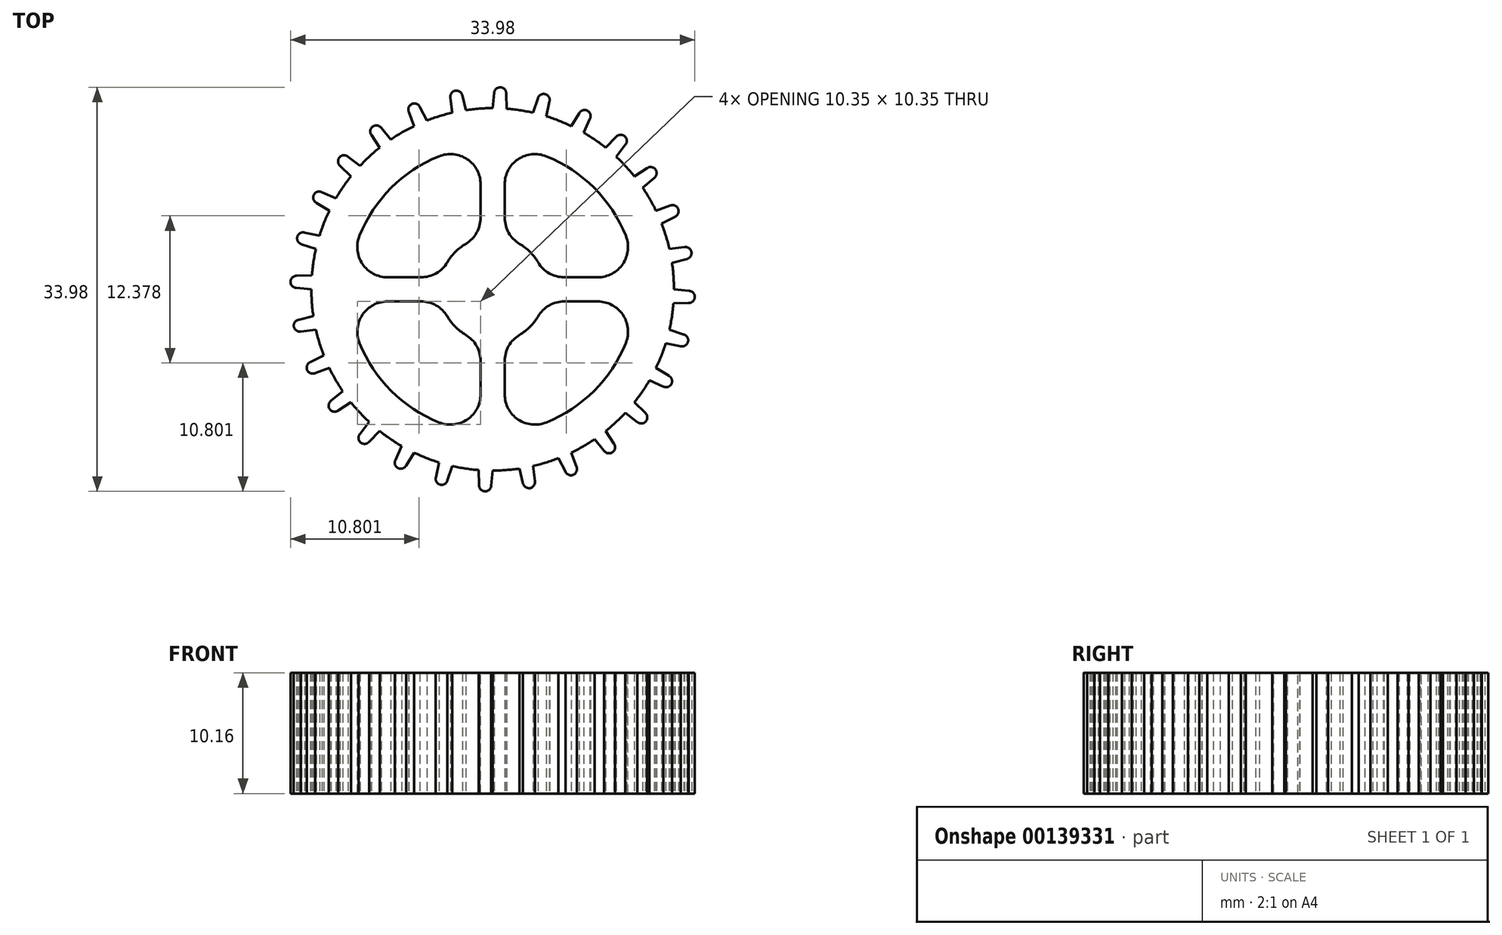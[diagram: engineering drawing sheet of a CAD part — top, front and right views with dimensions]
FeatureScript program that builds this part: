
annotation { "Feature Type Name" : "Feature", "Feature Type Description" : "" }
export const myFeature = defineFeature(function(context is Context, id is Id, definition is map)
    precondition{}
    {
        {
            var Q0;
            Q0=qCreatedBy(makeId("Top.planeOp"),FACE);
            var sketch = newSketch(context, id + "F0", { "sketchPlane" : qUnion([Q0])});
            skCircle(sketch, "E0", {"center": v(0, 0) * mm, "radius": 15.24 * mm});
            skLineSegment(sketch, "E1", {"start": v(0, 15.24) * mm, "end": v(1.17, 15.2) * mm});
            skLineSegment(sketch, "E2", {"start": v(1.17, 15.2) * mm, "end": v(1.14, 16.46) * mm});
            skLineSegment(sketch, "E3", {"start": v(0.13, 16.5) * mm, "end": v(0, 15.24) * mm});
            skArc(sketch, "E4", {"start": v(1.14, 16.46) * mm, "mid": v(0.65, 17) * mm, "end": v(0.13, 16.5) * mm});
            skLineSegment(sketch, "E5.1.0", {"start": v(-2.24, 15.07) * mm, "end": v(-2.55, 16.3) * mm});
            skArc(sketch, "E5.1.1", {"start": v(-2.55, 16.3) * mm, "mid": v(-3.14, 16.71) * mm, "end": v(-3.55, 16.12) * mm});
            skLineSegment(sketch, "E5.1.2", {"start": v(-3.55, 16.12) * mm, "end": v(-3.4, 14.86) * mm});
            skLineSegment(sketch, "E5.2.0", {"start": v(-5.54, 14.2) * mm, "end": v(-6.12, 15.33) * mm});
            skArc(sketch, "E5.2.1", {"start": v(-6.12, 15.33) * mm, "mid": v(-6.78, 15.6) * mm, "end": v(-7.05, 14.92) * mm});
            skLineSegment(sketch, "E5.2.2", {"start": v(-7.05, 14.92) * mm, "end": v(-6.61, 13.73) * mm});
            skLineSegment(sketch, "E5.3.0", {"start": v(-8.56, 12.6) * mm, "end": v(-9.37, 13.58) * mm});
            skArc(sketch, "E5.3.1", {"start": v(-9.37, 13.58) * mm, "mid": v(-10.08, 13.7) * mm, "end": v(-10.2, 12.98) * mm});
            skLineSegment(sketch, "E5.3.2", {"start": v(-10.2, 12.98) * mm, "end": v(-9.5, 11.92) * mm});
            skLineSegment(sketch, "E5.4.0", {"start": v(-11.15, 10.39) * mm, "end": v(-12.16, 11.16) * mm});
            skArc(sketch, "E5.4.1", {"start": v(-12.16, 11.16) * mm, "mid": v(-12.88, 11.1) * mm, "end": v(-12.82, 10.39) * mm});
            skLineSegment(sketch, "E5.4.2", {"start": v(-12.82, 10.39) * mm, "end": v(-11.92, 9.5) * mm});
            skLineSegment(sketch, "E5.5.0", {"start": v(-13.18, 7.65) * mm, "end": v(-14.34, 8.17) * mm});
            skArc(sketch, "E5.5.1", {"start": v(-14.34, 8.17) * mm, "mid": v(-15.03, 7.96) * mm, "end": v(-14.81, 7.27) * mm});
            skLineSegment(sketch, "E5.5.2", {"start": v(-14.81, 7.27) * mm, "end": v(-13.73, 6.61) * mm});
            skLineSegment(sketch, "E5.6.0", {"start": v(-14.55, 4.52) * mm, "end": v(-15.8, 4.78) * mm});
            skArc(sketch, "E5.6.1", {"start": v(-15.8, 4.78) * mm, "mid": v(-16.42, 4.42) * mm, "end": v(-16.06, 3.8) * mm});
            skLineSegment(sketch, "E5.6.2", {"start": v(-16.06, 3.8) * mm, "end": v(-14.86, 3.4) * mm});
            skLineSegment(sketch, "E5.7.0", {"start": v(-15.2, 1.17) * mm, "end": v(-16.46, 1.14) * mm});
            skArc(sketch, "E5.7.1", {"start": v(-16.46, 1.14) * mm, "mid": v(-17, 0.65) * mm, "end": v(-16.5, 0.13) * mm});
            skLineSegment(sketch, "E5.7.2", {"start": v(-16.5, 0.13) * mm, "end": v(-15.24, 0) * mm});
            skLineSegment(sketch, "E5.8.0", {"start": v(-15.07, -2.24) * mm, "end": v(-16.3, -2.55) * mm});
            skArc(sketch, "E5.8.1", {"start": v(-16.3, -2.55) * mm, "mid": v(-16.71, -3.14) * mm, "end": v(-16.12, -3.55) * mm});
            skLineSegment(sketch, "E5.8.2", {"start": v(-16.12, -3.55) * mm, "end": v(-14.86, -3.4) * mm});
            skLineSegment(sketch, "E5.9.0", {"start": v(-14.2, -5.54) * mm, "end": v(-15.33, -6.12) * mm});
            skArc(sketch, "E5.9.1", {"start": v(-15.33, -6.12) * mm, "mid": v(-15.6, -6.78) * mm, "end": v(-14.92, -7.05) * mm});
            skLineSegment(sketch, "E5.9.2", {"start": v(-14.92, -7.05) * mm, "end": v(-13.73, -6.61) * mm});
            skLineSegment(sketch, "E5.10.0", {"start": v(-12.6, -8.56) * mm, "end": v(-13.58, -9.37) * mm});
            skArc(sketch, "E5.10.1", {"start": v(-13.58, -9.37) * mm, "mid": v(-13.7, -10.08) * mm, "end": v(-12.98, -10.2) * mm});
            skLineSegment(sketch, "E5.10.2", {"start": v(-12.98, -10.2) * mm, "end": v(-11.92, -9.5) * mm});
            skLineSegment(sketch, "E5.11.0", {"start": v(-10.39, -11.15) * mm, "end": v(-11.16, -12.16) * mm});
            skArc(sketch, "E5.11.1", {"start": v(-11.16, -12.16) * mm, "mid": v(-11.1, -12.88) * mm, "end": v(-10.39, -12.82) * mm});
            skLineSegment(sketch, "E5.11.2", {"start": v(-10.39, -12.82) * mm, "end": v(-9.5, -11.92) * mm});
            skLineSegment(sketch, "E5.12.0", {"start": v(-7.65, -13.18) * mm, "end": v(-8.17, -14.34) * mm});
            skArc(sketch, "E5.12.1", {"start": v(-8.17, -14.34) * mm, "mid": v(-7.96, -15.03) * mm, "end": v(-7.27, -14.81) * mm});
            skLineSegment(sketch, "E5.12.2", {"start": v(-7.27, -14.81) * mm, "end": v(-6.61, -13.73) * mm});
            skLineSegment(sketch, "E5.13.0", {"start": v(-4.52, -14.55) * mm, "end": v(-4.78, -15.8) * mm});
            skArc(sketch, "E5.13.1", {"start": v(-4.78, -15.8) * mm, "mid": v(-4.42, -16.42) * mm, "end": v(-3.8, -16.06) * mm});
            skLineSegment(sketch, "E5.13.2", {"start": v(-3.8, -16.06) * mm, "end": v(-3.4, -14.86) * mm});
            skLineSegment(sketch, "E5.14.0", {"start": v(-1.17, -15.2) * mm, "end": v(-1.14, -16.46) * mm});
            skArc(sketch, "E5.14.1", {"start": v(-1.14, -16.46) * mm, "mid": v(-0.65, -17) * mm, "end": v(-0.13, -16.5) * mm});
            skLineSegment(sketch, "E5.14.2", {"start": v(-0.13, -16.5) * mm, "end": v(0, -15.24) * mm});
            skLineSegment(sketch, "E5.15.0", {"start": v(2.24, -15.07) * mm, "end": v(2.55, -16.3) * mm});
            skArc(sketch, "E5.15.1", {"start": v(2.55, -16.3) * mm, "mid": v(3.14, -16.71) * mm, "end": v(3.55, -16.12) * mm});
            skLineSegment(sketch, "E5.15.2", {"start": v(3.55, -16.12) * mm, "end": v(3.4, -14.86) * mm});
            skLineSegment(sketch, "E5.16.0", {"start": v(5.54, -14.2) * mm, "end": v(6.12, -15.33) * mm});
            skArc(sketch, "E5.16.1", {"start": v(6.12, -15.33) * mm, "mid": v(6.78, -15.6) * mm, "end": v(7.05, -14.92) * mm});
            skLineSegment(sketch, "E5.16.2", {"start": v(7.05, -14.92) * mm, "end": v(6.61, -13.73) * mm});
            skLineSegment(sketch, "E5.17.0", {"start": v(8.56, -12.6) * mm, "end": v(9.37, -13.58) * mm});
            skArc(sketch, "E5.17.1", {"start": v(9.37, -13.58) * mm, "mid": v(10.08, -13.7) * mm, "end": v(10.2, -12.98) * mm});
            skLineSegment(sketch, "E5.17.2", {"start": v(10.2, -12.98) * mm, "end": v(9.5, -11.92) * mm});
            skLineSegment(sketch, "E5.18.0", {"start": v(11.15, -10.39) * mm, "end": v(12.16, -11.16) * mm});
            skArc(sketch, "E5.18.1", {"start": v(12.16, -11.16) * mm, "mid": v(12.88, -11.1) * mm, "end": v(12.82, -10.39) * mm});
            skLineSegment(sketch, "E5.18.2", {"start": v(12.82, -10.39) * mm, "end": v(11.92, -9.5) * mm});
            skLineSegment(sketch, "E5.19.0", {"start": v(13.18, -7.65) * mm, "end": v(14.34, -8.17) * mm});
            skArc(sketch, "E5.19.1", {"start": v(14.34, -8.17) * mm, "mid": v(15.03, -7.96) * mm, "end": v(14.81, -7.27) * mm});
            skLineSegment(sketch, "E5.19.2", {"start": v(14.81, -7.27) * mm, "end": v(13.73, -6.61) * mm});
            skLineSegment(sketch, "E5.20.0", {"start": v(14.55, -4.52) * mm, "end": v(15.8, -4.78) * mm});
            skArc(sketch, "E5.20.1", {"start": v(15.8, -4.78) * mm, "mid": v(16.42, -4.42) * mm, "end": v(16.06, -3.8) * mm});
            skLineSegment(sketch, "E5.20.2", {"start": v(16.06, -3.8) * mm, "end": v(14.86, -3.4) * mm});
            skLineSegment(sketch, "E5.21.0", {"start": v(15.2, -1.17) * mm, "end": v(16.46, -1.14) * mm});
            skArc(sketch, "E5.21.1", {"start": v(16.46, -1.14) * mm, "mid": v(17, -0.65) * mm, "end": v(16.5, -0.13) * mm});
            skLineSegment(sketch, "E5.21.2", {"start": v(16.5, -0.13) * mm, "end": v(15.24, 0) * mm});
            skLineSegment(sketch, "E5.22.0", {"start": v(15.07, 2.24) * mm, "end": v(16.3, 2.55) * mm});
            skArc(sketch, "E5.22.1", {"start": v(16.3, 2.55) * mm, "mid": v(16.71, 3.14) * mm, "end": v(16.12, 3.55) * mm});
            skLineSegment(sketch, "E5.22.2", {"start": v(16.12, 3.55) * mm, "end": v(14.86, 3.4) * mm});
            skLineSegment(sketch, "E5.23.0", {"start": v(14.2, 5.54) * mm, "end": v(15.33, 6.12) * mm});
            skArc(sketch, "E5.23.1", {"start": v(15.33, 6.12) * mm, "mid": v(15.6, 6.78) * mm, "end": v(14.92, 7.05) * mm});
            skLineSegment(sketch, "E5.23.2", {"start": v(14.92, 7.05) * mm, "end": v(13.73, 6.61) * mm});
            skLineSegment(sketch, "E5.24.0", {"start": v(12.6, 8.56) * mm, "end": v(13.58, 9.37) * mm});
            skArc(sketch, "E5.24.1", {"start": v(13.58, 9.37) * mm, "mid": v(13.7, 10.08) * mm, "end": v(12.98, 10.2) * mm});
            skLineSegment(sketch, "E5.24.2", {"start": v(12.98, 10.2) * mm, "end": v(11.92, 9.5) * mm});
            skLineSegment(sketch, "E5.25.0", {"start": v(10.39, 11.15) * mm, "end": v(11.16, 12.16) * mm});
            skArc(sketch, "E5.25.1", {"start": v(11.16, 12.16) * mm, "mid": v(11.1, 12.88) * mm, "end": v(10.39, 12.82) * mm});
            skLineSegment(sketch, "E5.25.2", {"start": v(10.39, 12.82) * mm, "end": v(9.5, 11.92) * mm});
            skLineSegment(sketch, "E5.26.0", {"start": v(7.65, 13.18) * mm, "end": v(8.17, 14.34) * mm});
            skArc(sketch, "E5.26.1", {"start": v(8.17, 14.34) * mm, "mid": v(7.96, 15.03) * mm, "end": v(7.27, 14.81) * mm});
            skLineSegment(sketch, "E5.26.2", {"start": v(7.27, 14.81) * mm, "end": v(6.61, 13.73) * mm});
            skLineSegment(sketch, "E5.27.0", {"start": v(4.52, 14.55) * mm, "end": v(4.78, 15.8) * mm});
            skArc(sketch, "E5.27.1", {"start": v(4.78, 15.8) * mm, "mid": v(4.42, 16.42) * mm, "end": v(3.8, 16.06) * mm});
            skLineSegment(sketch, "E5.27.2", {"start": v(3.8, 16.06) * mm, "end": v(3.4, 14.86) * mm});
            skSolve(sketch);
        }
        {
            var Q0;
            Q0 = qSketchRegion(id + "F0", true);
            extrude(context, id + "F1", {"entities" : qUnion([Q0]), "depth" : 10.16 * mm});
        }
        {
            var Q0;
            Q0=makeQuery(id+"F1.opExtrude","CAP_FACE",FACE,{"disambiguationData":[OSD([sQuery(id+"F0.wireOp",EDGE,"E0"),sQuery(id+"F0.wireOp",EDGE,"E2"),sQuery(id+"F0.wireOp",EDGE,"E3"),sQuery(id+"F0.wireOp",EDGE,"E4"),sQuery(id+"F0.wireOp",EDGE,"E5.1.0"),sQuery(id+"F0.wireOp",EDGE,"E5.1.1"),sQuery(id+"F0.wireOp",EDGE,"E5.1.2"),sQuery(id+"F0.wireOp",EDGE,"E5.2.0"),sQuery(id+"F0.wireOp",EDGE,"E5.2.1"),sQuery(id+"F0.wireOp",EDGE,"E5.2.2"),sQuery(id+"F0.wireOp",EDGE,"E5.3.0"),sQuery(id+"F0.wireOp",EDGE,"E5.3.1"),sQuery(id+"F0.wireOp",EDGE,"E5.3.2"),sQuery(id+"F0.wireOp",EDGE,"E5.4.0"),sQuery(id+"F0.wireOp",EDGE,"E5.4.1"),sQuery(id+"F0.wireOp",EDGE,"E5.4.2"),sQuery(id+"F0.wireOp",EDGE,"E5.5.0"),sQuery(id+"F0.wireOp",EDGE,"E5.5.1"),sQuery(id+"F0.wireOp",EDGE,"E5.5.2"),sQuery(id+"F0.wireOp",EDGE,"E5.6.0"),sQuery(id+"F0.wireOp",EDGE,"E5.6.1"),sQuery(id+"F0.wireOp",EDGE,"E5.6.2"),sQuery(id+"F0.wireOp",EDGE,"E5.7.0"),sQuery(id+"F0.wireOp",EDGE,"E5.7.1"),sQuery(id+"F0.wireOp",EDGE,"E5.7.2"),sQuery(id+"F0.wireOp",EDGE,"E5.8.0"),sQuery(id+"F0.wireOp",EDGE,"E5.8.1"),sQuery(id+"F0.wireOp",EDGE,"E5.8.2"),sQuery(id+"F0.wireOp",EDGE,"E5.9.0"),sQuery(id+"F0.wireOp",EDGE,"E5.9.1"),sQuery(id+"F0.wireOp",EDGE,"E5.9.2"),sQuery(id+"F0.wireOp",EDGE,"E5.10.0"),sQuery(id+"F0.wireOp",EDGE,"E5.10.1"),sQuery(id+"F0.wireOp",EDGE,"E5.10.2"),sQuery(id+"F0.wireOp",EDGE,"E5.11.0"),sQuery(id+"F0.wireOp",EDGE,"E5.11.1"),sQuery(id+"F0.wireOp",EDGE,"E5.11.2"),sQuery(id+"F0.wireOp",EDGE,"E5.12.0"),sQuery(id+"F0.wireOp",EDGE,"E5.12.1"),sQuery(id+"F0.wireOp",EDGE,"E5.12.2"),sQuery(id+"F0.wireOp",EDGE,"E5.13.0"),sQuery(id+"F0.wireOp",EDGE,"E5.13.1"),sQuery(id+"F0.wireOp",EDGE,"E5.13.2"),sQuery(id+"F0.wireOp",EDGE,"E5.14.0"),sQuery(id+"F0.wireOp",EDGE,"E5.14.1"),sQuery(id+"F0.wireOp",EDGE,"E5.14.2"),sQuery(id+"F0.wireOp",EDGE,"E5.15.0"),sQuery(id+"F0.wireOp",EDGE,"E5.15.1"),sQuery(id+"F0.wireOp",EDGE,"E5.15.2"),sQuery(id+"F0.wireOp",EDGE,"E5.16.0"),sQuery(id+"F0.wireOp",EDGE,"E5.16.1"),sQuery(id+"F0.wireOp",EDGE,"E5.16.2"),sQuery(id+"F0.wireOp",EDGE,"E5.17.0"),sQuery(id+"F0.wireOp",EDGE,"E5.17.1"),sQuery(id+"F0.wireOp",EDGE,"E5.17.2"),sQuery(id+"F0.wireOp",EDGE,"E5.18.0"),sQuery(id+"F0.wireOp",EDGE,"E5.18.1"),sQuery(id+"F0.wireOp",EDGE,"E5.18.2"),sQuery(id+"F0.wireOp",EDGE,"E5.19.0"),sQuery(id+"F0.wireOp",EDGE,"E5.19.1"),sQuery(id+"F0.wireOp",EDGE,"E5.19.2"),sQuery(id+"F0.wireOp",EDGE,"E5.20.0"),sQuery(id+"F0.wireOp",EDGE,"E5.20.1"),sQuery(id+"F0.wireOp",EDGE,"E5.20.2"),sQuery(id+"F0.wireOp",EDGE,"E5.21.0"),sQuery(id+"F0.wireOp",EDGE,"E5.21.1"),sQuery(id+"F0.wireOp",EDGE,"E5.21.2"),sQuery(id+"F0.wireOp",EDGE,"E5.22.0"),sQuery(id+"F0.wireOp",EDGE,"E5.22.1"),sQuery(id+"F0.wireOp",EDGE,"E5.22.2"),sQuery(id+"F0.wireOp",EDGE,"E5.23.0"),sQuery(id+"F0.wireOp",EDGE,"E5.23.1"),sQuery(id+"F0.wireOp",EDGE,"E5.23.2"),sQuery(id+"F0.wireOp",EDGE,"E5.24.0"),sQuery(id+"F0.wireOp",EDGE,"E5.24.1"),sQuery(id+"F0.wireOp",EDGE,"E5.24.2"),sQuery(id+"F0.wireOp",EDGE,"E5.25.0"),sQuery(id+"F0.wireOp",EDGE,"E5.25.1"),sQuery(id+"F0.wireOp",EDGE,"E5.25.2"),sQuery(id+"F0.wireOp",EDGE,"E5.26.0"),sQuery(id+"F0.wireOp",EDGE,"E5.26.1"),sQuery(id+"F0.wireOp",EDGE,"E5.26.2"),sQuery(id+"F0.wireOp",EDGE,"E5.27.0"),sQuery(id+"F0.wireOp",EDGE,"E5.27.1"),sQuery(id+"F0.wireOp",EDGE,"E5.27.2"),sQuery(id+"F0.wireOp",EDGE,"E5.28.0"),sQuery(id+"F0.wireOp",EDGE,"E5.28.1"),sQuery(id+"F0.wireOp",EDGE,"E5.28.2"),sQuery(id+"F0.wireOp",EDGE,"E5.29.0"),sQuery(id+"F0.wireOp",EDGE,"E5.29.1"),sQuery(id+"F0.wireOp",EDGE,"E5.29.2"),sQuery(id+"F0.wireOp",EDGE,"E5.30.0"),sQuery(id+"F0.wireOp",EDGE,"E5.30.1"),sQuery(id+"F0.wireOp",EDGE,"E5.30.2"),sQuery(id+"F0.wireOp",EDGE,"E5.31.0"),sQuery(id+"F0.wireOp",EDGE,"E5.31.1"),sQuery(id+"F0.wireOp",EDGE,"E5.31.2"),sQuery(id+"F0.wireOp",EDGE,"E5.32.0"),sQuery(id+"F0.wireOp",EDGE,"E5.32.1"),sQuery(id+"F0.wireOp",EDGE,"E5.32.2"),sQuery(id+"F0.wireOp",EDGE,"E5.33.0"),sQuery(id+"F0.wireOp",EDGE,"E5.33.1"),sQuery(id+"F0.wireOp",EDGE,"E5.33.2"),sQuery(id+"F0.wireOp",EDGE,"E5.34.0"),sQuery(id+"F0.wireOp",EDGE,"E5.34.1"),sQuery(id+"F0.wireOp",EDGE,"E5.34.2"),sQuery(id+"F0.wireOp",EDGE,"E5.35.0"),sQuery(id+"F0.wireOp",EDGE,"E5.35.1"),sQuery(id+"F0.wireOp",EDGE,"E5.35.2")])],"isStart":false});
            var sketch = newSketch(context, id + "F2", { "sketchPlane" : qUnion([Q0])});
            skArc(sketch, "E6", {"start": v(-1.02, 12.02) * mm, "mid": v(-8.53, 8.53) * mm, "end": v(-12.02, 1.02) * mm});
            skArc(sketch, "E7", {"start": v(-1.02, 4.33) * mm, "mid": v(-3.14, 3.14) * mm, "end": v(-4.33, 1.02) * mm});
            skLineSegment(sketch, "E8", {"start": v(-1.02, 4.33) * mm, "end": v(-1.02, 12.02) * mm});
            skLineSegment(sketch, "E9", {"start": v(1.02, 4.33) * mm, "end": v(1.02, 12.02) * mm});
            skLineSegment(sketch, "E10", {"start": v(-4.33, 1.02) * mm, "end": v(-12.02, 1.02) * mm});
            skLineSegment(sketch, "E11", {"start": v(-4.33, -1.02) * mm, "end": v(-12.02, -1.02) * mm});
            skLineSegment(sketch, "E12", {"start": v(-1.02, -4.33) * mm, "end": v(-1.02, -12.02) * mm});
            skLineSegment(sketch, "E13", {"start": v(1.02, -4.33) * mm, "end": v(1.02, -12.02) * mm});
            skLineSegment(sketch, "E14", {"start": v(4.33, 1.02) * mm, "end": v(12.02, 1.02) * mm});
            skLineSegment(sketch, "E15", {"start": v(4.33, -1.02) * mm, "end": v(12.02, -1.02) * mm});
            skArc(sketch, "E16.trimOffspring", {"start": v(4.33, 1.02) * mm, "mid": v(3.14, 3.14) * mm, "end": v(1.02, 4.33) * mm});
            skArc(sketch, "E17.trimOffspring", {"start": v(1.02, -4.33) * mm, "mid": v(3.14, -3.14) * mm, "end": v(4.33, -1.02) * mm});
            skArc(sketch, "E18.trimOffspring", {"start": v(-4.33, -1.02) * mm, "mid": v(-3.14, -3.14) * mm, "end": v(-1.02, -4.33) * mm});
            skArc(sketch, "E19.trimOffspring", {"start": v(12.02, 1.02) * mm, "mid": v(8.53, 8.53) * mm, "end": v(1.02, 12.02) * mm});
            skArc(sketch, "E20.trimOffspring", {"start": v(1.02, -12.02) * mm, "mid": v(8.53, -8.53) * mm, "end": v(12.02, -1.02) * mm});
            skArc(sketch, "E21.trimOffspring", {"start": v(-12.02, -1.02) * mm, "mid": v(-8.53, -8.53) * mm, "end": v(-1.02, -12.02) * mm});
            skSolve(sketch);
        }
        {
            var Q0;
            Q0 = qSketchRegion(id + "F2", true);
            extrude(context, id + "F3", {"entities" : qUnion([Q0]), "operationType" : NewBodyOperationType.REMOVE, "oppositeDirection" : true, "depth" : 25.4 * mm});
        }
        {
            var Q0;
            Q0=makeQuery(id+"F3.boolean.opBoolean","COPY",EDGE,{"derivedFrom":makeQuery(id+"F3.opExtrude","SWEPT_EDGE",EDGE,{"disambiguationData":[OSD([sQuery(id+"F2.wireOp",EDGE,"E9"),sQuery(id+"F2.wireOp",EDGE,"E16.trimOffspring")])]})});
            var Q1;
            Q1=makeQuery(id+"F3.boolean.opBoolean","COPY",EDGE,{"derivedFrom":makeQuery(id+"F3.opExtrude","SWEPT_EDGE",EDGE,{"disambiguationData":[OSD([sQuery(id+"F2.wireOp",EDGE,"E14"),sQuery(id+"F2.wireOp",EDGE,"E16.trimOffspring")])]})});
            var Q2;
            Q2=makeQuery(id+"F3.boolean.opBoolean","COPY",EDGE,{"derivedFrom":makeQuery(id+"F3.opExtrude","SWEPT_EDGE",EDGE,{"disambiguationData":[OSD([sQuery(id+"F2.wireOp",EDGE,"E9"),sQuery(id+"F2.wireOp",EDGE,"E19.trimOffspring")])]})});
            var Q3;
            Q3=makeQuery(id+"F3.boolean.opBoolean","COPY",EDGE,{"derivedFrom":makeQuery(id+"F3.opExtrude","SWEPT_EDGE",EDGE,{"disambiguationData":[OSD([sQuery(id+"F2.wireOp",EDGE,"E14"),sQuery(id+"F2.wireOp",EDGE,"E19.trimOffspring")])]})});
            var Q4;
            Q4=makeQuery(id+"F3.boolean.opBoolean","COPY",EDGE,{"derivedFrom":makeQuery(id+"F3.opExtrude","SWEPT_EDGE",EDGE,{"disambiguationData":[OSD([sQuery(id+"F2.wireOp",EDGE,"E13"),sQuery(id+"F2.wireOp",EDGE,"E17.trimOffspring")])]})});
            var Q5;
            Q5=makeQuery(id+"F3.boolean.opBoolean","COPY",EDGE,{"derivedFrom":makeQuery(id+"F3.opExtrude","SWEPT_EDGE",EDGE,{"disambiguationData":[OSD([sQuery(id+"F2.wireOp",EDGE,"E15"),sQuery(id+"F2.wireOp",EDGE,"E17.trimOffspring")])]})});
            var Q6;
            Q6=makeQuery(id+"F3.boolean.opBoolean","COPY",EDGE,{"derivedFrom":makeQuery(id+"F3.opExtrude","SWEPT_EDGE",EDGE,{"disambiguationData":[OSD([sQuery(id+"F2.wireOp",EDGE,"E15"),sQuery(id+"F2.wireOp",EDGE,"E20.trimOffspring")])]})});
            var Q7;
            Q7=makeQuery(id+"F3.boolean.opBoolean","COPY",EDGE,{"derivedFrom":makeQuery(id+"F3.opExtrude","SWEPT_EDGE",EDGE,{"disambiguationData":[OSD([sQuery(id+"F2.wireOp",EDGE,"E13"),sQuery(id+"F2.wireOp",EDGE,"E20.trimOffspring")])]})});
            var Q8;
            Q8=makeQuery(id+"F3.boolean.opBoolean","COPY",EDGE,{"derivedFrom":makeQuery(id+"F3.opExtrude","SWEPT_EDGE",EDGE,{"disambiguationData":[OSD([sQuery(id+"F2.wireOp",EDGE,"E11"),sQuery(id+"F2.wireOp",EDGE,"E18.trimOffspring")])]})});
            var Q9;
            Q9=makeQuery(id+"F3.boolean.opBoolean","COPY",EDGE,{"derivedFrom":makeQuery(id+"F3.opExtrude","SWEPT_EDGE",EDGE,{"disambiguationData":[OSD([sQuery(id+"F2.wireOp",EDGE,"E12"),sQuery(id+"F2.wireOp",EDGE,"E18.trimOffspring")])]})});
            var Q10;
            Q10=makeQuery(id+"F3.boolean.opBoolean","COPY",EDGE,{"derivedFrom":makeQuery(id+"F3.opExtrude","SWEPT_EDGE",EDGE,{"disambiguationData":[OSD([sQuery(id+"F2.wireOp",EDGE,"E11"),sQuery(id+"F2.wireOp",EDGE,"E21.trimOffspring")])]})});
            var Q11;
            Q11=makeQuery(id+"F3.boolean.opBoolean","COPY",EDGE,{"derivedFrom":makeQuery(id+"F3.opExtrude","SWEPT_EDGE",EDGE,{"disambiguationData":[OSD([sQuery(id+"F2.wireOp",EDGE,"E6"),sQuery(id+"F2.wireOp",EDGE,"E8")])]})});
            var Q12;
            Q12=makeQuery(id+"F3.boolean.opBoolean","COPY",EDGE,{"derivedFrom":makeQuery(id+"F3.opExtrude","SWEPT_EDGE",EDGE,{"disambiguationData":[OSD([sQuery(id+"F2.wireOp",EDGE,"E7"),sQuery(id+"F2.wireOp",EDGE,"E8")])]})});
            var Q13;
            Q13=makeQuery(id+"F3.boolean.opBoolean","COPY",EDGE,{"derivedFrom":makeQuery(id+"F3.opExtrude","SWEPT_EDGE",EDGE,{"disambiguationData":[OSD([sQuery(id+"F2.wireOp",EDGE,"E7"),sQuery(id+"F2.wireOp",EDGE,"E10")])]})});
            var Q14;
            Q14=makeQuery(id+"F3.boolean.opBoolean","COPY",EDGE,{"derivedFrom":makeQuery(id+"F3.opExtrude","SWEPT_EDGE",EDGE,{"disambiguationData":[OSD([sQuery(id+"F2.wireOp",EDGE,"E6"),sQuery(id+"F2.wireOp",EDGE,"E10")])]})});
            var Q15;
            Q15=makeQuery(id+"F3.boolean.opBoolean","COPY",EDGE,{"derivedFrom":makeQuery(id+"F3.opExtrude","SWEPT_EDGE",EDGE,{"disambiguationData":[OSD([sQuery(id+"F2.wireOp",EDGE,"E12"),sQuery(id+"F2.wireOp",EDGE,"E21.trimOffspring")])]})});
            fillet(context, id + "F4", {"entities" : qUnion([Q0, Q1, Q2, Q3, Q4, Q5, Q6, Q7, Q8, Q9, Q10, Q11, Q12, Q13, Q14, Q15]), "radius" : 2.54 * mm, "tangentPropagation" : true, "allowEdgeOverflow" : false});
        }
    });
